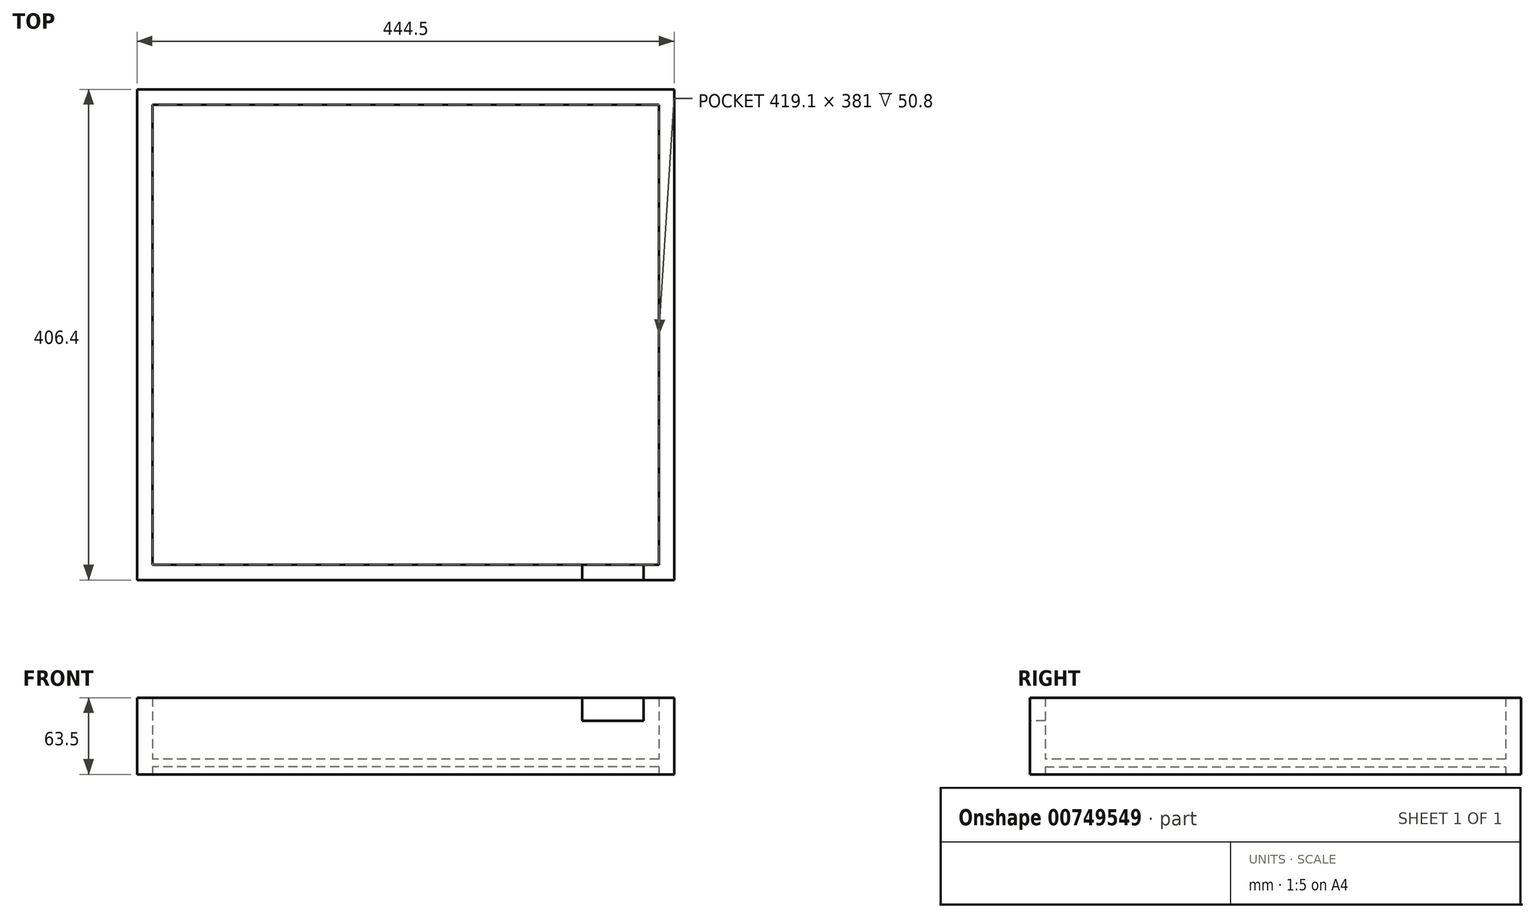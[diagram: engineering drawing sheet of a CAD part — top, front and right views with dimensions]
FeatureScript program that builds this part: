
annotation { "Feature Type Name" : "Feature", "Feature Type Description" : "" }
export const myFeature = defineFeature(function(context is Context, id is Id, definition is map)
    precondition{}
    {
        {
            var Q0;
            Q0=qCreatedBy(makeId("Top.planeOp"),FACE);
            var sketch = newSketch(context, id + "F0", { "sketchPlane" : qUnion([Q0])});
            skLineSegment(sketch, "E0.bottom", {"start": v(222.25, 203.2) * mm, "end": v(-222.25, 203.2) * mm});
            skLineSegment(sketch, "E0.top", {"start": v(222.25, -203.2) * mm, "end": v(-222.25, -203.2) * mm});
            skLineSegment(sketch, "E0.left", {"start": v(222.25, 203.2) * mm, "end": v(222.25, -203.2) * mm});
            skLineSegment(sketch, "E0.right", {"start": v(-222.25, 203.2) * mm, "end": v(-222.25, -203.2) * mm});
            skPoint(sketch, "E0.middle", {"position": v(0, 0) * mm});
            skLineSegment(sketch, "E1.bottom", {"start": v(209.55, 190.5) * mm, "end": v(-209.55, 190.5) * mm});
            skLineSegment(sketch, "E1.top", {"start": v(209.55, -190.5) * mm, "end": v(-209.55, -190.5) * mm});
            skLineSegment(sketch, "E1.left", {"start": v(209.55, 190.5) * mm, "end": v(209.55, -190.5) * mm});
            skLineSegment(sketch, "E1.right", {"start": v(-209.55, 190.5) * mm, "end": v(-209.55, -190.5) * mm});
            skSolve(sketch);
        }
        {
            var Q0;
            Q0=makeQuery(id+"F0.imprint","IMPRINT",FACE,{"disambiguationData":[TD([[makeQuery(id+"F0.imprint","IMPRINT",EDGE,{"derivedFrom":sQuery(id+"F0.wireOp",EDGE,"E0.bottom")}),1.0]])]});
            extrude(context, id + "F1", {"entities" : qUnion([Q0]), "depth" : 63.5 * mm, "offsetDistance" : 25.4 * mm});
        }
        {
            var Q0;
            Q0=makeQuery(id+"F1.opExtrude","CAP_FACE",FACE,{"disambiguationData":[OSD([sQuery(id+"F0.wireOp",EDGE,"E0.bottom"),sQuery(id+"F0.wireOp",EDGE,"E0.top"),sQuery(id+"F0.wireOp",EDGE,"E0.left"),sQuery(id+"F0.wireOp",EDGE,"E0.right"),sQuery(id+"F0.wireOp",EDGE,"E1.bottom"),sQuery(id+"F0.wireOp",EDGE,"E1.top"),sQuery(id+"F0.wireOp",EDGE,"E1.left"),sQuery(id+"F0.wireOp",EDGE,"E1.right")])],"isStart":true});
            var sketch = newSketch(context, id + "F2", { "sketchPlane" : qUnion([Q0])});
            skLineSegment(sketch, "E2.bottom", {"start": v(-209.55, 190.5) * mm, "end": v(209.55, 190.5) * mm});
            skLineSegment(sketch, "E2.top", {"start": v(-209.55, -190.5) * mm, "end": v(209.55, -190.5) * mm});
            skLineSegment(sketch, "E2.left", {"start": v(-209.55, 190.5) * mm, "end": v(-209.55, -190.5) * mm});
            skLineSegment(sketch, "E2.right", {"start": v(209.55, 190.5) * mm, "end": v(209.55, -190.5) * mm});
            skPoint(sketch, "E2.middle", {"position": v(0, 0) * mm});
            skSolve(sketch);
        }
        {
            var Q0;
            Q0=makeQuery(id+"F2.imprint","IMPRINT",FACE,{"disambiguationData":[TD([[makeQuery(id+"F2.imprint","IMPRINT",EDGE,{"derivedFrom":sQuery(id+"F2.wireOp",EDGE,"E2.bottom")}),1.0]])]});
            extrude(context, id + "F3", {"entities" : qUnion([Q0]), "operationType" : NewBodyOperationType.ADD, "oppositeDirection" : true, "depth" : 12.7 * mm, "offsetDistance" : 25.4 * mm});
        }
        {
            var Q0;
            Q0=makeQuery(id+"F3.boolean.opBoolean","MERGE",FACE,{"derivedFrom":[makeQuery(id+"F1.opExtrude","CAP_FACE",FACE,{"disambiguationData":[OSD([sQuery(id+"F0.wireOp",EDGE,"E0.bottom"),sQuery(id+"F0.wireOp",EDGE,"E0.top"),sQuery(id+"F0.wireOp",EDGE,"E0.left"),sQuery(id+"F0.wireOp",EDGE,"E0.right"),sQuery(id+"F0.wireOp",EDGE,"E1.bottom"),sQuery(id+"F0.wireOp",EDGE,"E1.top"),sQuery(id+"F0.wireOp",EDGE,"E1.left"),sQuery(id+"F0.wireOp",EDGE,"E1.right")])],"isStart":true}),makeQuery(id+"F3.opExtrude","CAP_FACE",FACE,{"disambiguationData":[OSD([sQuery(id+"F2.wireOp",EDGE,"E2.bottom"),sQuery(id+"F2.wireOp",EDGE,"E2.top"),sQuery(id+"F2.wireOp",EDGE,"E2.left"),sQuery(id+"F2.wireOp",EDGE,"E2.right")])],"isStart":true})]});
            var sketch = newSketch(context, id + "F4", { "sketchPlane" : qUnion([Q0])});
            skLineSegment(sketch, "E3.bottom", {"start": v(209.55, 190.5) * mm, "end": v(-209.55, 190.5) * mm});
            skLineSegment(sketch, "E3.top", {"start": v(209.55, -190.5) * mm, "end": v(-209.55, -190.5) * mm});
            skLineSegment(sketch, "E3.left", {"start": v(209.55, 190.5) * mm, "end": v(209.55, -190.5) * mm});
            skLineSegment(sketch, "E3.right", {"start": v(-209.55, 190.5) * mm, "end": v(-209.55, -190.5) * mm});
            skPoint(sketch, "E3.middle", {"position": v(0, 0) * mm});
            skSolve(sketch);
        }
        {
            var Q0;
            Q0=makeQuery(id+"F4.imprint","IMPRINT",FACE,{"disambiguationData":[TD([[makeQuery(id+"F4.imprint","IMPRINT",EDGE,{"derivedFrom":sQuery(id+"F4.wireOp",EDGE,"E3.bottom")}),1.0]])]});
            extrude(context, id + "F5", {"entities" : qUnion([Q0]), "operationType" : NewBodyOperationType.REMOVE, "oppositeDirection" : true, "depth" : 6.35 * mm, "offsetDistance" : 25.4 * mm});
        }
        {
            var Q0;
            Q0=makeQuery(id+"F1.opExtrude","SWEPT_FACE",FACE,{"disambiguationData":[OSD([sQuery(id+"F0.wireOp",EDGE,"E0.top")])]});
            var sketch = newSketch(context, id + "F6", { "sketchPlane" : qUnion([Q0])});
            skLineSegment(sketch, "E4", {"start": v(222.25, 63.5) * mm, "end": v(196.85, 63.5) * mm});
            skLineSegment(sketch, "E5.bottom", {"start": v(196.85, 63.5) * mm, "end": v(146.05, 63.5) * mm});
            skLineSegment(sketch, "E5.top", {"start": v(196.85, 44.45) * mm, "end": v(146.05, 44.45) * mm});
            skLineSegment(sketch, "E5.left", {"start": v(196.85, 63.5) * mm, "end": v(196.85, 44.45) * mm});
            skLineSegment(sketch, "E5.right", {"start": v(146.05, 63.5) * mm, "end": v(146.05, 44.45) * mm});
            skSolve(sketch);
        }
        {
            var Q0;
            Q0=makeQuery(id+"F6.imprint","IMPRINT",FACE,{"disambiguationData":[TD([[makeQuery(id+"F6.imprint","IMPRINT",EDGE,{"derivedFrom":sQuery(id+"F6.wireOp",EDGE,"E5.bottom")}),1.0]])]});
            extrude(context, id + "F7", {"entities" : qUnion([Q0]), "operationType" : NewBodyOperationType.REMOVE, "oppositeDirection" : true, "depth" : 25.4 * mm, "offsetDistance" : 25.4 * mm});
        }
    });
